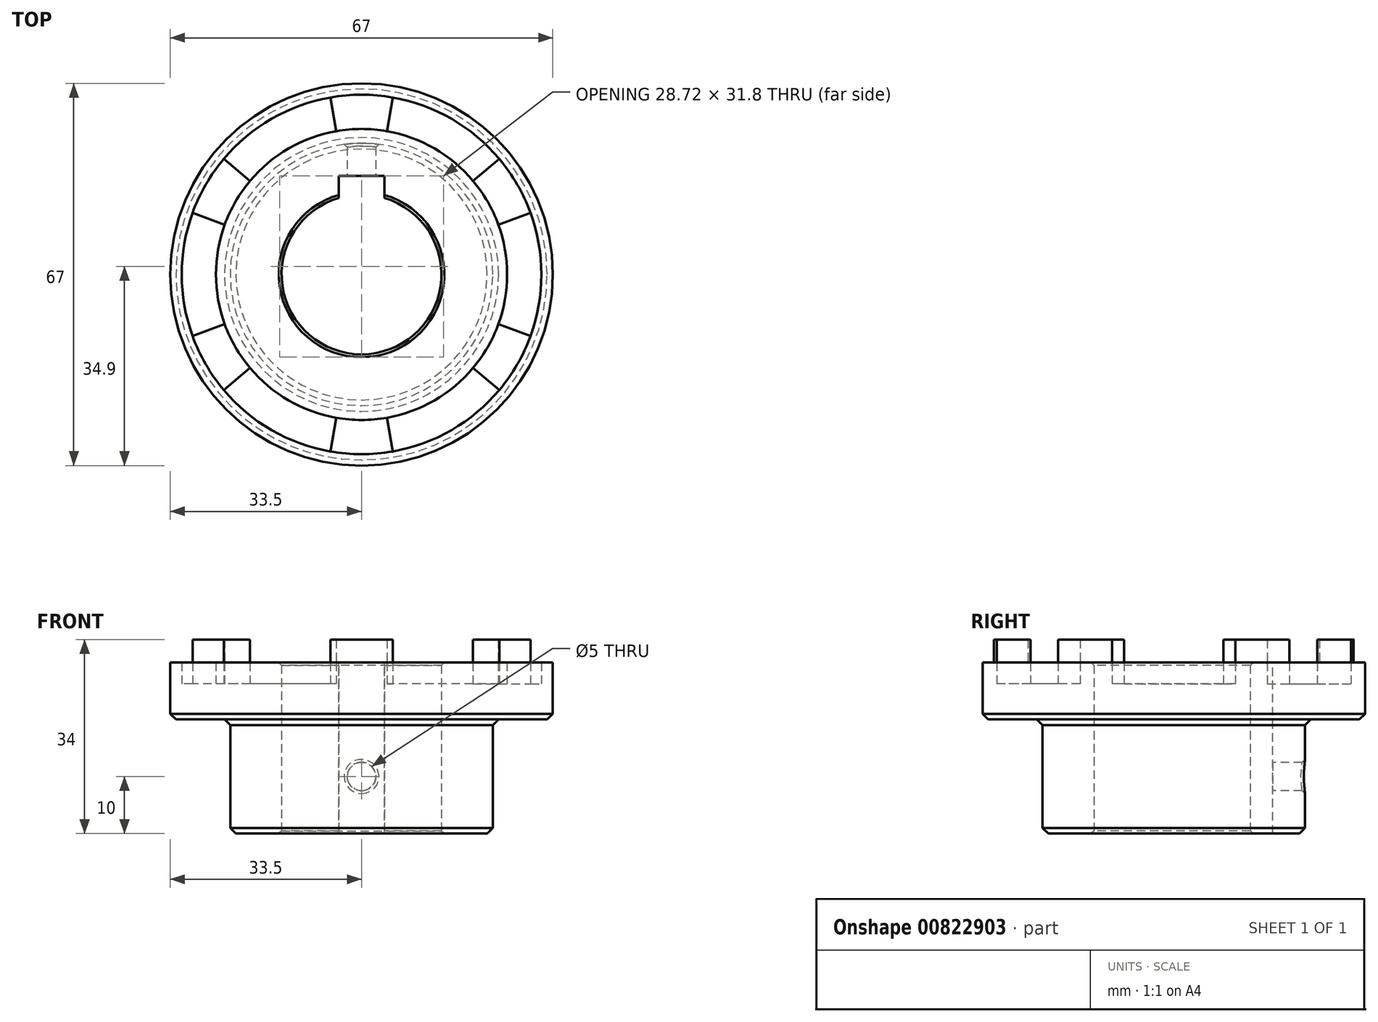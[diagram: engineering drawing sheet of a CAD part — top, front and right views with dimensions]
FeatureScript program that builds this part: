
annotation { "Feature Type Name" : "Feature", "Feature Type Description" : "" }
export const myFeature = defineFeature(function(context is Context, id is Id, definition is map)
    precondition{}
    {
        {
            var Q0;
            Q0=qCreatedBy(makeId("Front.planeOp"),FACE);
            var sketch = newSketch(context, id + "F0", { "sketchPlane" : qUnion([Q0])});
            skLineSegment(sketch, "E0", {"start": v(0, 0) * mm, "end": v(-14, 0) * mm, "construction": true});
            skLineSegment(sketch, "E1", {"start": v(-14, 0) * mm, "end": v(-14, 30) * mm});
            skLineSegment(sketch, "E2", {"start": v(-14, 30) * mm, "end": v(-25.5, 30) * mm});
            skLineSegment(sketch, "E3", {"start": v(-25.5, 30) * mm, "end": v(-25.5, 26.25) * mm});
            skLineSegment(sketch, "E4", {"start": v(-25.5, 26.25) * mm, "end": v(-31.5, 26.25) * mm});
            skLineSegment(sketch, "E5", {"start": v(-31.5, 26.25) * mm, "end": v(-31.5, 30) * mm});
            skLineSegment(sketch, "E6", {"start": v(-31.5, 30) * mm, "end": v(-33.5, 30) * mm});
            skLineSegment(sketch, "E7", {"start": v(-33.5, 30) * mm, "end": v(-33.5, 20) * mm});
            skLineSegment(sketch, "E8", {"start": v(-33.5, 20) * mm, "end": v(-23, 20) * mm});
            skLineSegment(sketch, "E9", {"start": v(-23, 20) * mm, "end": v(-23, 0) * mm});
            skLineSegment(sketch, "E10", {"start": v(-23, 0) * mm, "end": v(-14, 0) * mm});
            skLineSegment(sketch, "E11", {"start": v(0, 0) * mm, "end": v(0, 30) * mm, "construction": true});
            skSolve(sketch);
        }
        {
            var Q0;
            Q0=makeQuery(id+"F0.imprint","IMPRINT",FACE,{"disambiguationData":[TD([[makeQuery(id+"F0.imprint","IMPRINT",EDGE,{"derivedFrom":sQuery(id+"F0.wireOp",EDGE,"E1")}),1.0]])]});
            var Q1;
            Q1=sQuery(id+"F0.wireOp",EDGE,"E11");
            revolve(context, id + "F1", {"surfaceOperationType" : NewSurfaceOperationType.NEW, "entities" : qUnion([Q0]), "axis" : qUnion([Q1]), "revolveType" : RevolveType.FULL});
        }
        {
            var Q0;
            Q0=makeQuery(id+"F1.opRevolve","SWEPT_FACE",FACE,{"disambiguationData":[OSD([sQuery(id+"F0.wireOp",EDGE,"E8")])]});
            var Q1;
            Q1=makeQuery(id+"F1.opRevolve","SWEPT_EDGE",EDGE,{"disambiguationData":[OSD([sQuery(id+"F0.wireOp",EDGE,"E9"),sQuery(id+"F0.wireOp",EDGE,"E10")])]});
            chamfer(context, id + "F2", {"entities" : qUnion([Q0, Q1]), "width" : 1 * mm, "tangentPropagation" : true});
        }
        {
            var Q0;
            Q0=makeQuery(id+"F1.opRevolve","SWEPT_FACE",FACE,{"disambiguationData":[OSD([sQuery(id+"F0.wireOp",EDGE,"E1")])]});
            chamfer(context, id + "F3", {"entities" : qUnion([Q0]), "width" : 0.5 * mm, "tangentPropagation" : true});
        }
        {
            var Q0;
            Q0=makeQuery(id+"F1.opRevolve","SWEPT_FACE",FACE,{"disambiguationData":[OSD([sQuery(id+"F0.wireOp",EDGE,"E4")])]});
            var sketch = newSketch(context, id + "F4", { "sketchPlane" : qUnion([Q0])});
            skLineSegment(sketch, "E12", {"start": v(0, 0) * mm, "end": v(10.27, 0) * mm, "construction": true});
            skLineSegment(sketch, "E13.1.0", {"start": v(0, 0) * mm, "end": v(0, 10.27) * mm, "construction": true});
            skLineSegment(sketch, "E13.2.0", {"start": v(0, 0) * mm, "end": v(-10.27, 0) * mm, "construction": true});
            skLineSegment(sketch, "E13.3.0", {"start": v(0, 0) * mm, "end": v(0, -10.27) * mm, "construction": true});
            skPoint(sketch, "E13.center", {"position": v(0, 0) * mm});
            skLineSegment(sketch, "E14", {"start": v(0, 0) * mm, "end": v(47.61, 27.49) * mm, "construction": true});
            skLineSegment(sketch, "E15", {"start": v(19.53, 16.4) * mm, "end": v(24.13, 20.25) * mm});
            skLineSegment(sketch, "E16.MirrorCS", {"start": v(23.96, 8.72) * mm, "end": v(29.6, 10.77) * mm});
            skArc(sketch, "E17.0", {"start": v(23.96, 8.72) * mm, "mid": v(22.08, 12.75) * mm, "end": v(19.53, 16.4) * mm});
            skPoint(sketch, "E18.orphan", {"position": v(30.04, 25.2) * mm});
            skPoint(sketch, "E19.orphan", {"position": v(36.85, 13.41) * mm});
            skArc(sketch, "E20.0", {"start": v(29.6, 10.77) * mm, "mid": v(27.28, 15.75) * mm, "end": v(24.13, 20.25) * mm});
            skArc(sketch, "E21.1.0", {"start": v(4.43, 25.11) * mm, "mid": v(0, 25.5) * mm, "end": v(-4.43, 25.11) * mm});
            skLineSegment(sketch, "E21.1.1", {"start": v(-4.43, 25.11) * mm, "end": v(-5.47, 31.02) * mm});
            skLineSegment(sketch, "E21.1.2", {"start": v(4.43, 25.11) * mm, "end": v(5.47, 31.02) * mm});
            skArc(sketch, "E21.1.3", {"start": v(5.47, 31.02) * mm, "mid": v(0, 31.5) * mm, "end": v(-5.47, 31.02) * mm});
            skArc(sketch, "E21.2.0", {"start": v(-19.53, 16.4) * mm, "mid": v(-22.08, 12.75) * mm, "end": v(-23.96, 8.72) * mm});
            skLineSegment(sketch, "E21.2.1", {"start": v(-23.96, 8.72) * mm, "end": v(-29.6, 10.77) * mm});
            skLineSegment(sketch, "E21.2.2", {"start": v(-19.53, 16.4) * mm, "end": v(-24.13, 20.25) * mm});
            skArc(sketch, "E21.2.3", {"start": v(-24.13, 20.25) * mm, "mid": v(-27.28, 15.75) * mm, "end": v(-29.6, 10.77) * mm});
            skArc(sketch, "E21.3.0", {"start": v(-23.96, -8.72) * mm, "mid": v(-22.08, -12.75) * mm, "end": v(-19.53, -16.4) * mm});
            skLineSegment(sketch, "E21.3.1", {"start": v(-19.53, -16.4) * mm, "end": v(-24.13, -20.25) * mm});
            skLineSegment(sketch, "E21.3.2", {"start": v(-23.96, -8.72) * mm, "end": v(-29.6, -10.77) * mm});
            skArc(sketch, "E21.3.3", {"start": v(-29.6, -10.77) * mm, "mid": v(-27.28, -15.75) * mm, "end": v(-24.13, -20.25) * mm});
            skArc(sketch, "E21.4.0", {"start": v(-4.43, -25.11) * mm, "mid": v(0, -25.5) * mm, "end": v(4.43, -25.11) * mm});
            skLineSegment(sketch, "E21.4.1", {"start": v(4.43, -25.11) * mm, "end": v(5.47, -31.02) * mm});
            skLineSegment(sketch, "E21.4.2", {"start": v(-4.43, -25.11) * mm, "end": v(-5.47, -31.02) * mm});
            skArc(sketch, "E21.4.3", {"start": v(-5.47, -31.02) * mm, "mid": v(0, -31.5) * mm, "end": v(5.47, -31.02) * mm});
            skArc(sketch, "E21.5.0", {"start": v(19.53, -16.4) * mm, "mid": v(22.08, -12.75) * mm, "end": v(23.96, -8.72) * mm});
            skLineSegment(sketch, "E21.5.1", {"start": v(23.96, -8.72) * mm, "end": v(29.6, -10.77) * mm});
            skLineSegment(sketch, "E21.5.2", {"start": v(19.53, -16.4) * mm, "end": v(24.13, -20.25) * mm});
            skArc(sketch, "E21.5.3", {"start": v(24.13, -20.25) * mm, "mid": v(27.28, -15.75) * mm, "end": v(29.6, -10.77) * mm});
            skSolve(sketch);
        }
        {
            var Q0;
            Q0=qSketchRegion(id+"F4",true);
            extrude(context, id + "F5", {"entities" : qUnion([Q0]), "operationType" : NewBodyOperationType.ADD, "depth" : 7.75 * mm, "offsetDistance" : 25 * mm});
        }
        {
            var Q0;
            Q0=makeQuery(id+"F1.opRevolve","SWEPT_FACE",FACE,{"disambiguationData":[OSD([sQuery(id+"F0.wireOp",EDGE,"E2")])]});
            var sketch = newSketch(context, id + "F6", { "sketchPlane" : qUnion([Q0])});
            skLineSegment(sketch, "E22", {"start": v(0, 0) * mm, "end": v(13.63, 0) * mm, "construction": true});
            skLineSegment(sketch, "E23.1.0", {"start": v(0, 0) * mm, "end": v(0, 13.63) * mm, "construction": true});
            skLineSegment(sketch, "E23.2.0", {"start": v(0, 0) * mm, "end": v(-13.63, 0) * mm, "construction": true});
            skLineSegment(sketch, "E23.3.0", {"start": v(0, 0) * mm, "end": v(0, -13.63) * mm, "construction": true});
            skPoint(sketch, "E23.center", {"position": v(0, 0) * mm});
            skLineSegment(sketch, "E24.bottom", {"start": v(4, 17.3) * mm, "end": v(-4, 17.3) * mm});
            skLineSegment(sketch, "E24.top", {"start": v(4, 10.3) * mm, "end": v(-4, 10.3) * mm});
            skLineSegment(sketch, "E24.left", {"start": v(4, 17.3) * mm, "end": v(4, 10.3) * mm});
            skLineSegment(sketch, "E24.right", {"start": v(-4, 17.3) * mm, "end": v(-4, 10.3) * mm});
            skPoint(sketch, "E24.middle", {"position": v(0, 13.8) * mm});
            skCircle(sketch, "E25.0", {"center": v(0, 0) * mm, "radius": 14 * mm, "construction": true});
            skPoint(sketch, "E26", {"position": v(0, -14) * mm});
            skSolve(sketch);
        }
        {
            var Q0;
            Q0=qSketchRegion(id+"F6",true);
            extrude(context, id + "F7", {"entities" : qUnion([Q0]), "operationType" : NewBodyOperationType.REMOVE, "endBound" : BoundingType.UP_TO_NEXT, "oppositeDirection" : true, "depth" : 25 * mm, "offsetDistance" : 25 * mm});
        }
        {
            var Q0;
            Q0=qCreatedBy(makeId("Front.planeOp"),FACE);
            var sketch = newSketch(context, id + "F8", { "sketchPlane" : qUnion([Q0])});
            skLineSegment(sketch, "E27", {"start": v(0, 0) * mm, "end": v(0, 10) * mm, "construction": true});
            skCircle(sketch, "E28", {"center": v(0, 10) * mm, "radius": 2.5 * mm});
            skSolve(sketch);
        }
        {
            var Q0;
            Q0=makeQuery(id+"F8.imprint","IMPRINT",FACE,{"disambiguationData":[TD([[makeQuery(id+"F8.imprint","IMPRINT",EDGE,{"derivedFrom":sQuery(id+"F8.wireOp",EDGE,"E28")}),1.0]])]});
            extrude(context, id + "F9", {"entities" : qUnion([Q0]), "operationType" : NewBodyOperationType.REMOVE, "oppositeDirection" : true, "depth" : 25 * mm, "offsetDistance" : 25 * mm});
        }
        {
            var Q0;
            Q0=makeQuery(id+"F9.boolean.opBoolean","INTERSECT",EDGE,{"derivedFrom":[makeQuery(id+"F1.opRevolve","SWEPT_FACE",FACE,{"disambiguationData":[OSD([sQuery(id+"F0.wireOp",EDGE,"E9")])]}),makeQuery(id+"F9.opExtrude","SWEPT_FACE",FACE,{"disambiguationData":[OSD([sQuery(id+"F8.wireOp",EDGE,"E28")])]})]});
            chamfer(context, id + "F10", {"entities" : qUnion([Q0]), "width" : 0.5 * mm, "tangentPropagation" : true});
        }
    });
